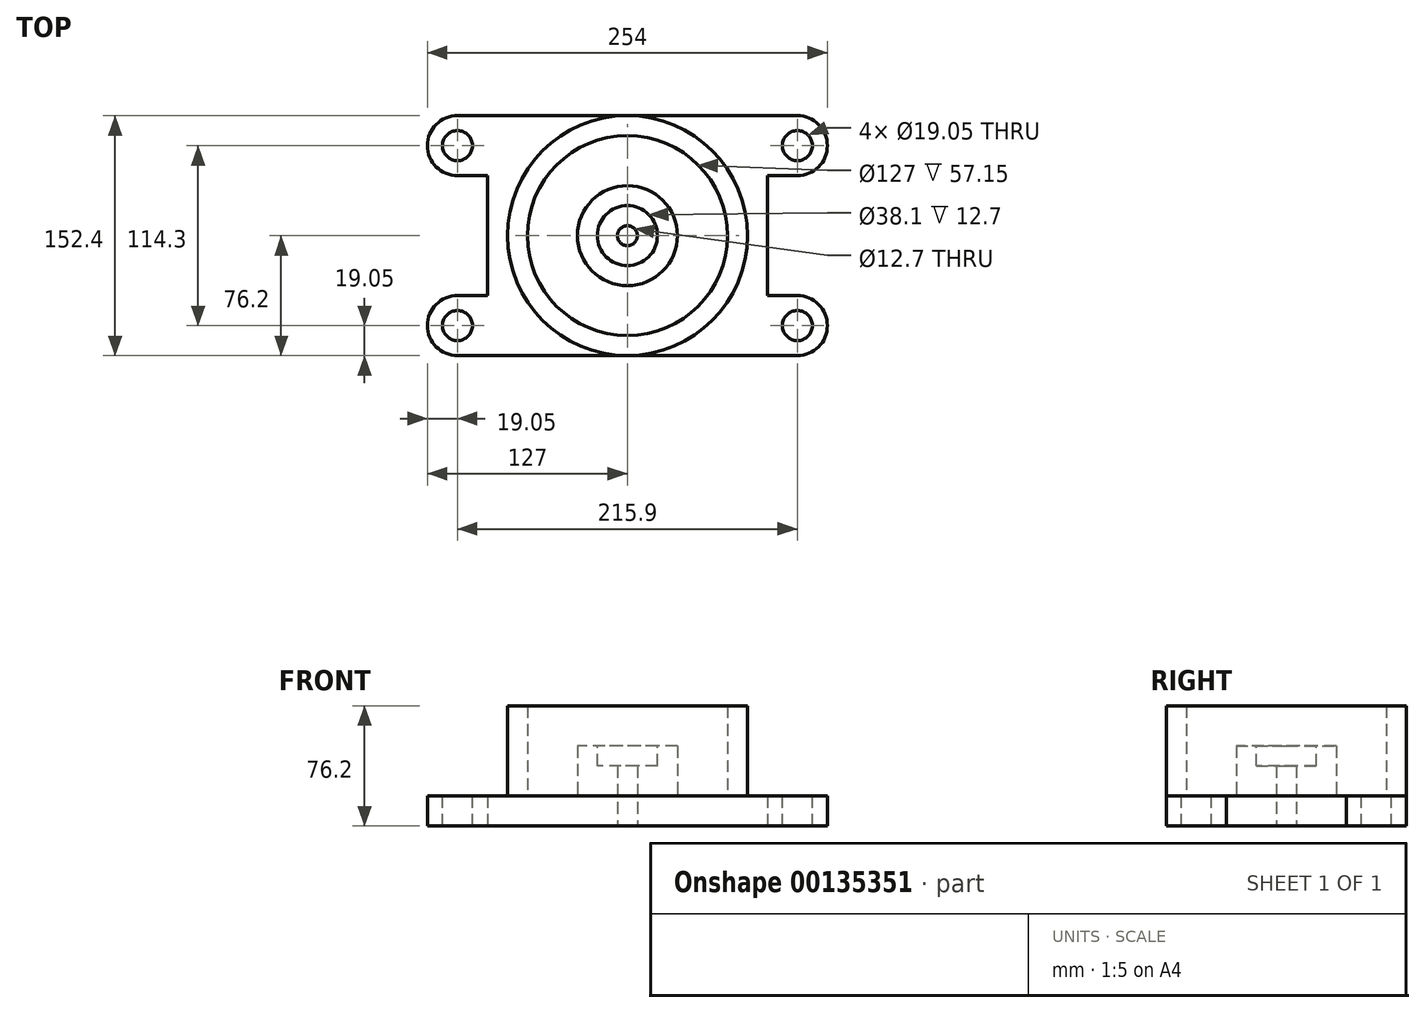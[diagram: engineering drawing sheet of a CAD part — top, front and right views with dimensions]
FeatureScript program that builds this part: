
annotation { "Feature Type Name" : "Feature", "Feature Type Description" : "" }
export const myFeature = defineFeature(function(context is Context, id is Id, definition is map)
    precondition{}
    {
        {
            var Q0;
            Q0=qCreatedBy(makeId("Top.planeOp"),FACE);
            var sketch = newSketch(context, id + "F0", { "sketchPlane" : qUnion([Q0])});
            skCircle(sketch, "E0", {"center": v(0, 0) * mm, "radius": 76.2 * mm});
            skCircle(sketch, "E1", {"center": v(0, 0) * mm, "radius": 63.5 * mm});
            skLineSegment(sketch, "E2", {"start": v(0, -76.2) * mm, "end": v(-127, -76.2) * mm});
            skLineSegment(sketch, "E3", {"start": v(-127, -76.2) * mm, "end": v(-127, -38.1) * mm});
            skLineSegment(sketch, "E4", {"start": v(-127, -38.1) * mm, "end": v(-88.9, -38.1) * mm});
            skLineSegment(sketch, "E5", {"start": v(0, 76.2) * mm, "end": v(0, -63.5) * mm, "construction": true});
            skLineSegment(sketch, "E6.MirrorCS", {"start": v(127, -38.1) * mm, "end": v(88.9, -38.1) * mm});
            skLineSegment(sketch, "E7.MirrorCS", {"start": v(0, -76.2) * mm, "end": v(127, -76.2) * mm});
            skLineSegment(sketch, "E8.MirrorCS", {"start": v(127, -76.2) * mm, "end": v(127, -38.1) * mm});
            skLineSegment(sketch, "E9", {"start": v(0, 76.2) * mm, "end": v(-127, 76.2) * mm});
            skLineSegment(sketch, "E10", {"start": v(0, 76.2) * mm, "end": v(127, 76.2) * mm});
            skLineSegment(sketch, "E11", {"start": v(-88.9, -38.1) * mm, "end": v(-88.9, 38.1) * mm});
            skLineSegment(sketch, "E12", {"start": v(127, 76.2) * mm, "end": v(127, 38.1) * mm});
            skLineSegment(sketch, "E13", {"start": v(127, 38.1) * mm, "end": v(88.9, 38.1) * mm});
            skLineSegment(sketch, "E14", {"start": v(88.9, -38.1) * mm, "end": v(88.9, 38.1) * mm});
            skLineSegment(sketch, "E15", {"start": v(-127, 76.2) * mm, "end": v(-127, 38.1) * mm});
            skLineSegment(sketch, "E16", {"start": v(-127, 38.1) * mm, "end": v(-88.9, 38.1) * mm});
            skLineSegment(sketch, "E17", {"start": v(0, 76.2) * mm, "end": v(0, -76.2) * mm, "construction": true});
            skCircle(sketch, "E18", {"center": v(0, 0) * mm, "radius": 31.75 * mm});
            skCircle(sketch, "E19", {"center": v(0, 0) * mm, "radius": 19.05 * mm});
            skCircle(sketch, "E20", {"center": v(0, 0) * mm, "radius": 6.35 * mm});
            skSolve(sketch);
        }
        {
            var Q0;
            Q0=makeQuery(id+"F0.imprint","IMPRINT",FACE,{"disambiguationData":[TD([[makeQuery(id+"F0.imprint","IMPRINT",EDGE,{"derivedFrom":sQuery(id+"F0.wireOp",EDGE,"E6.MirrorCS")}),1.0]])]});
            extrude(context, id + "F1", {"entities" : qUnion([Q0]), "depth" : 19.05 * mm});
        }
        {
            var Q0;
            Q0=makeQuery(id+"F0.imprint","IMPRINT",FACE,{"disambiguationData":[TD([[makeQuery(id+"F0.imprint","IMPRINT",EDGE,{"derivedFrom":sQuery(id+"F0.wireOp",EDGE,"E1")}),-1.0]])]});
            extrude(context, id + "F2", {"entities" : qUnion([Q0]), "operationType" : NewBodyOperationType.ADD, "depth" : 76.2 * mm});
        }
        {
            var Q0;
            Q0=makeQuery(id+"F0.imprint","IMPRINT",FACE,{"disambiguationData":[TD([[makeQuery(id+"F0.imprint","IMPRINT",EDGE,{"derivedFrom":sQuery(id+"F0.wireOp",EDGE,"E1")}),1.0]])]});
            extrude(context, id + "F3", {"entities" : qUnion([Q0]), "operationType" : NewBodyOperationType.ADD, "depth" : 19.05 * mm});
        }
        {
            var Q0;
            Q0=makeQuery(id+"F0.imprint","IMPRINT",FACE,{"disambiguationData":[TD([[makeQuery(id+"F0.imprint","IMPRINT",EDGE,{"derivedFrom":sQuery(id+"F0.wireOp",EDGE,"E18")}),1.0]])]});
            var Q1;
            Q1=makeQuery(id+"F0.imprint","IMPRINT",FACE,{"disambiguationData":[TD([[makeQuery(id+"F0.imprint","IMPRINT",EDGE,{"derivedFrom":sQuery(id+"F0.wireOp",EDGE,"E19")}),1.0]])]});
            var Q2;
            Q2=makeQuery(id+"F0.imprint","IMPRINT",FACE,{"disambiguationData":[TD([[makeQuery(id+"F0.imprint","IMPRINT",EDGE,{"derivedFrom":sQuery(id+"F0.wireOp",EDGE,"E20")}),1.0]])]});
            extrude(context, id + "F4", {"entities" : qUnion([Q0, Q1, Q2]), "operationType" : NewBodyOperationType.ADD, "depth" : 50.8 * mm});
        }
        {
            var Q0;
            Q0=makeQuery(id+"F4.opExtrude","CAP_FACE",FACE,{"disambiguationData":[OSD([sQuery(id+"F0.wireOp",EDGE,"E18")])],"isStart":false});
            var sketch = newSketch(context, id + "F5", { "sketchPlane" : qUnion([Q0])});
            skCircle(sketch, "E21.0", {"center": v(0, 0) * mm, "radius": 19.05 * mm});
            skSolve(sketch);
        }
        {
            var Q0;
            Q0 = qSketchRegion(id + "F5", true);
            extrude(context, id + "F6", {"entities" : qUnion([Q0]), "operationType" : NewBodyOperationType.REMOVE, "oppositeDirection" : true, "depth" : 12.7 * mm});
        }
        {
            var Q0;
            Q0=makeQuery(id+"F0.imprint","IMPRINT",FACE,{"disambiguationData":[TD([[makeQuery(id+"F0.imprint","IMPRINT",EDGE,{"derivedFrom":sQuery(id+"F0.wireOp",EDGE,"E20")}),1.0]])]});
            extrude(context, id + "F7", {"entities" : qUnion([Q0]), "operationType" : NewBodyOperationType.REMOVE, "endBound" : BoundingType.THROUGH_ALL, "depth" : 25.4 * mm});
        }
        {
            var Q0;
            {var subQ0=sQuery(id+"F0.wireOp",EDGE,"E2");Q0=makeQuery(id+"F0.imprint","IMPRINT",FACE,{"disambiguationData":[TD([[makeQuery(id+"F0.imprint","IMPRINT",EDGE,{"derivedFrom":subQ0}),-1.0]])]});}
            extrude(context, id + "F8", {"entities" : qUnion([Q0]), "operationType" : NewBodyOperationType.ADD, "depth" : 19.05 * mm});
        }
        {
            var Q0;
            Q0=makeQuery(id+"F8.opExtrude","SWEPT_EDGE",EDGE,{"disambiguationData":[OSD([sQuery(id+"F0.wireOp",EDGE,"E2"),sQuery(id+"F0.wireOp",EDGE,"E3")])]});
            var Q1;
            Q1=makeQuery(id+"F8.opExtrude","SWEPT_EDGE",EDGE,{"disambiguationData":[OSD([sQuery(id+"F0.wireOp",EDGE,"E3"),sQuery(id+"F0.wireOp",EDGE,"E4")])]});
            var Q2;
            Q2=makeQuery(id+"F8.opExtrude","SWEPT_EDGE",EDGE,{"disambiguationData":[OSD([sQuery(id+"F0.wireOp",EDGE,"E15"),sQuery(id+"F0.wireOp",EDGE,"E16")])]});
            var Q3;
            Q3=makeQuery(id+"F8.opExtrude","SWEPT_EDGE",EDGE,{"disambiguationData":[OSD([sQuery(id+"F0.wireOp",EDGE,"E9"),sQuery(id+"F0.wireOp",EDGE,"E15")])]});
            var Q4;
            Q4=makeQuery(id+"F1.opExtrude","SWEPT_EDGE",EDGE,{"disambiguationData":[OSD([sQuery(id+"F0.wireOp",EDGE,"E12"),sQuery(id+"F0.wireOp",EDGE,"E13")])]});
            var Q5;
            Q5=makeQuery(id+"F1.opExtrude","SWEPT_EDGE",EDGE,{"disambiguationData":[OSD([sQuery(id+"F0.wireOp",EDGE,"E10"),sQuery(id+"F0.wireOp",EDGE,"E12")])]});
            var Q6;
            Q6=makeQuery(id+"F1.opExtrude","SWEPT_EDGE",EDGE,{"disambiguationData":[OSD([sQuery(id+"F0.wireOp",EDGE,"E7.MirrorCS"),sQuery(id+"F0.wireOp",EDGE,"E8.MirrorCS")])]});
            var Q7;
            Q7=makeQuery(id+"F1.opExtrude","SWEPT_EDGE",EDGE,{"disambiguationData":[OSD([sQuery(id+"F0.wireOp",EDGE,"E6.MirrorCS"),sQuery(id+"F0.wireOp",EDGE,"E8.MirrorCS")])]});
            fillet(context, id + "F9", {"entities" : qUnion([Q0, Q1, Q2, Q3, Q4, Q5, Q6, Q7]), "radius" : 19.05 * mm, "tangentPropagation" : true, "allowEdgeOverflow" : false});
        }
        {
            var Q0;
            Q0=makeQuery(id+"F8.opExtrude","CAP_FACE",FACE,{"disambiguationData":[OSD([sQuery(id+"F0.wireOp",EDGE,"E0"),sQuery(id+"F0.wireOp",EDGE,"E2"),sQuery(id+"F0.wireOp",EDGE,"E3"),sQuery(id+"F0.wireOp",EDGE,"E4"),sQuery(id+"F0.wireOp",EDGE,"E9"),sQuery(id+"F0.wireOp",EDGE,"E11"),sQuery(id+"F0.wireOp",EDGE,"E15"),sQuery(id+"F0.wireOp",EDGE,"E16")])],"isStart":false});
            var sketch = newSketch(context, id + "F10", { "sketchPlane" : qUnion([Q0])});
            skArc(sketch, "E22.0", {"start": v(-107.95, 76.2) * mm, "mid": v(-127, 57.15) * mm, "end": v(-107.95, 38.1) * mm});
            skArc(sketch, "E23.0", {"start": v(-107.95, -38.1) * mm, "mid": v(-127, -57.15) * mm, "end": v(-107.95, -76.2) * mm});
            skCircle(sketch, "E24", {"center": v(-107.95, -57.15) * mm, "radius": 9.53 * mm});
            skCircle(sketch, "E25", {"center": v(-107.95, 57.15) * mm, "radius": 9.53 * mm});
            skLineSegment(sketch, "E26.0", {"start": v(0, 76.2) * mm, "end": v(0, -63.5) * mm});
            skCircle(sketch, "E27.MirrorC", {"center": v(107.95, 57.15) * mm, "radius": 9.53 * mm});
            skCircle(sketch, "E28.MirrorC", {"center": v(107.95, -57.15) * mm, "radius": 9.53 * mm});
            skSolve(sketch);
        }
        {
            var Q0;
            Q0 = qSketchRegion(id + "F10", true);
            var Q1;
            {var subQ0=sQuery(id+"F0.wireOp",EDGE,"E0");var subQ1=sQuery(id+"F0.wireOp",EDGE,"E18");var subQ2=sQuery(id+"F0.wireOp",EDGE,"E1");Q1=makeQuery(id+"F8.boolean.opBoolean","MERGE",FACE,{"derivedFrom":[makeQuery(id+"F4.boolean.opBoolean","MERGE",FACE,{"derivedFrom":[makeQuery(id+"F3.boolean.opBoolean","MERGE",FACE,{"derivedFrom":[makeQuery(id+"F2.boolean.opBoolean","MERGE",FACE,{"derivedFrom":[makeQuery(id+"F1.opExtrude","CAP_FACE",FACE,{"disambiguationData":[OSD([subQ0,sQuery(id+"F0.wireOp",EDGE,"E6.MirrorCS"),sQuery(id+"F0.wireOp",EDGE,"E7.MirrorCS"),sQuery(id+"F0.wireOp",EDGE,"E8.MirrorCS"),sQuery(id+"F0.wireOp",EDGE,"E10"),sQuery(id+"F0.wireOp",EDGE,"E12"),sQuery(id+"F0.wireOp",EDGE,"E13"),sQuery(id+"F0.wireOp",EDGE,"E14")])],"isStart":true}),makeQuery(id+"F2.opExtrude","CAP_FACE",FACE,{"disambiguationData":[OSD([subQ0,subQ2])],"isStart":true})]}),makeQuery(id+"F3.opExtrude","CAP_FACE",FACE,{"disambiguationData":[OSD([subQ2,subQ1])],"isStart":true})]}),makeQuery(id+"F4.opExtrude","CAP_FACE",FACE,{"disambiguationData":[OSD([subQ1])],"isStart":true})]}),makeQuery(id+"F8.opExtrude","CAP_FACE",FACE,{"disambiguationData":[OSD([subQ0,sQuery(id+"F0.wireOp",EDGE,"E2"),sQuery(id+"F0.wireOp",EDGE,"E3"),sQuery(id+"F0.wireOp",EDGE,"E4"),sQuery(id+"F0.wireOp",EDGE,"E9"),sQuery(id+"F0.wireOp",EDGE,"E11"),sQuery(id+"F0.wireOp",EDGE,"E15"),sQuery(id+"F0.wireOp",EDGE,"E16")])],"isStart":true})]});}
            extrude(context, id + "F11", {"entities" : qUnion([Q0]), "operationType" : NewBodyOperationType.REMOVE, "endBound" : BoundingType.UP_TO_SURFACE, "oppositeDirection" : true, "endBoundEntityFace" : qUnion([Q1]), "depth" : 25.4 * mm});
        }
    });
